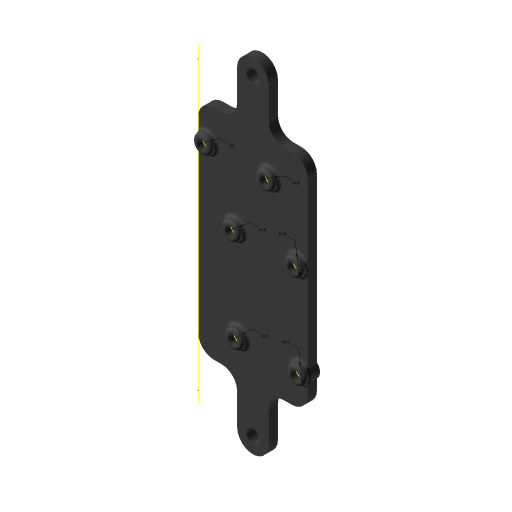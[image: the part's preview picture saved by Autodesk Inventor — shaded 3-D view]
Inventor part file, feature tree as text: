
AUTODESK INVENTOR PART (.ipt)
format: ipt  version: 2023 (Build 270158000, 158)  size: 293,888 bytes
history: native  units: mm
features: extrude x4, sketch x2, fillet x2
ambient origin geometry x8: Origin, YZ Plane, XZ Plane, XY Plane, X Axis, Y Axis, Z Axis, Center Point
bodies: Solid1 (feature_tree)
feature tree (8):
  extrude  "Extrusion1"  Depth=15.0mm
  sketch  "Sketch2"  dims[d0=35.0mm d12=15.0mm]
  extrude  "Extrusion2"  Depth=5.0mm
  extrude  "Extrusion3"  TaperAngle=0.0deg  [1 undecoded]
  fillet  "Fillet1"  Radius=3.0mm
  extrude  "Extrusion4"  Depth=3.0mm
  fillet  "Fillet4"  Radius=22.5mm
  sketch  "Sketch3"  dims[d13=55.0mm d14=2.5mm d15=0.0mm d16=3.0mm d17=3.0mm d18=22.5mm d19=12.0mm d20=13.0mm d21=52.0mm d22=3.3mm d23=3.3mm d24=3.3mm d25=20.0mm d27=20.0mm d28=10.0mm d30=10.0mm d32=3.0mm d33=0.0mm d34=6.0mm d35=6.0mm d36=6.0mm d37=6.0mm d38=6.0mm d39=6.0mm d40=2.0mm d41=0.0mm d42=3.0mm d43=0.0mm d44=1.0mm d45=4.4mm d46=4.4mm d47=100.0mm d48=10.0mm d49=10.0mm d52=15.0mm d53=15.0mm d54=15.0mm d55=15.0mm d56=0.0mm d57=0.0mm d58=5.0mm]
note: 1 required parameter value undecoded (feature->parameter linkage not recoverable at this tier; creation-order binding heuristic only, values carry confidence <= 0.55)
